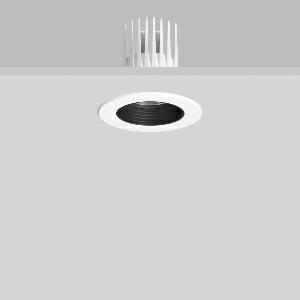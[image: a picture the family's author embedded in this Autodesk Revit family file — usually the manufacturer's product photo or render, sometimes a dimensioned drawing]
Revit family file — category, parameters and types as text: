
# Revit family: heledon_mini_e_901754_002_1_2564
name_source: partatom
category: Lighting Fixtures
units: mm (PartAtom-declared; Revit-internal decimal feet)

## family parameters
Cut with Voids When Loaded = No
Host = Face
Light Source = No
Part Type = Normal
Room Calculation Point = No
Round Connector Dimension = Use Diameter
Shared = No

## types (1)
- HELEDON mini E (1 x LED Modul 940, 3500 lm, 4000)
    Apparent Load = 29 VA
    Approval mark = CE
    CIE Flux Codes = 80 99 100 100 100
    Color Rendering = 92
    Color Temperature = 4000
    Default Elevation = 1800 mm
    Description = Series: HELEDON mini
Round recessed downlight. Housing: die-cast aluminium, powder-coated. Black plastic ring and recessed LED to prevent glare from the side. Optical assembly with lens made of plastic (polycarbonate) for the best homogeneous light distribution - can be changed without tools. Best colour rendering index Ra>90. Suitable for Recessed ceiling mounting. Installation without tools thanks to spring fastening system. Including separate LED converter with connecting cable 600 mm.High quality converter without flickering and stroboscopic effect. Through-wiring box (5 pole) available as accessory. The following accessories can be mounted without use of tools: interchangeable lenses, decorative glasses, honeycomb louvre, clear and frosted diffusers, white interchangeable plastic ring. 
Colour: traffic white, matt (RAL 9016)
Diameter: 124 mm
Height: 3 mm
Cut-out diameter: 114 mm
Recess height: 170 mm
Luminaire: recess height: 120 mm
Lamp: LED
Socket: without socket
Colour temperature: 4000K
Colour rendering index (CRI): 92
System power: 29 W
Rated luminous flux: 3500 lm
Luminous efficiency: 121 lm/W
Control gear: Regulated power supply
Protection class: II
Type of protection: IP 20
    Height = 0 mm  [stored 0 ft]
    Lamp = 1 x LED Modul 940
    Lamp Light Flux = 3500 lm
    Lamp count = 1
    Length = 124 mm
    Lifetime = 50000 h
    Luminous efficacy = 121 lm/W
    Manufacturer = RZB
    ModVariant = No
    Model = 901754.002.1
    Mounting Place = Ceiling
    Mounting Type = Recessed
    Number of Poles = 1
    OnlyDefault = Yes
    Power Factor = 1
    Product Name = HELEDON mini E
    Product group = Recessed downlights
    ProductGroupID = 402
    Protection Class = Protection class II
    Protection Degree = IP 20
    RLX_Detail_Level = 1
    RLX_Emergency_Light_Flux = 0 lm
    RLX_Emergency_Type = 0
    RLX_Emergency_Type_DB = No
    RlxData = <blob elided: 125213 chars, md5=02b6d770>
    Socket = socket
    Standby Power = 0 W
    System Light Flux = 3500 lm
    System Power = 29 W
    Type Comments = Product without accessories
    Type Image = 901656.002.jpg
    URL = http://relux.com
    VarID = ---
    Voltage = 230 V
    Voltage Range = 220-240 V
    Weight = 0.00 kg
    Width = 0 mm  [stored 0 ft]

note: [stored X ft] marks values corroborated as IEEE doubles in the binary element streams (Revit-internal decimal feet)

## geometry (parser evidence)
native form markers: Blend x4, Sweep x11
no freeform markers — native parametric forms only
